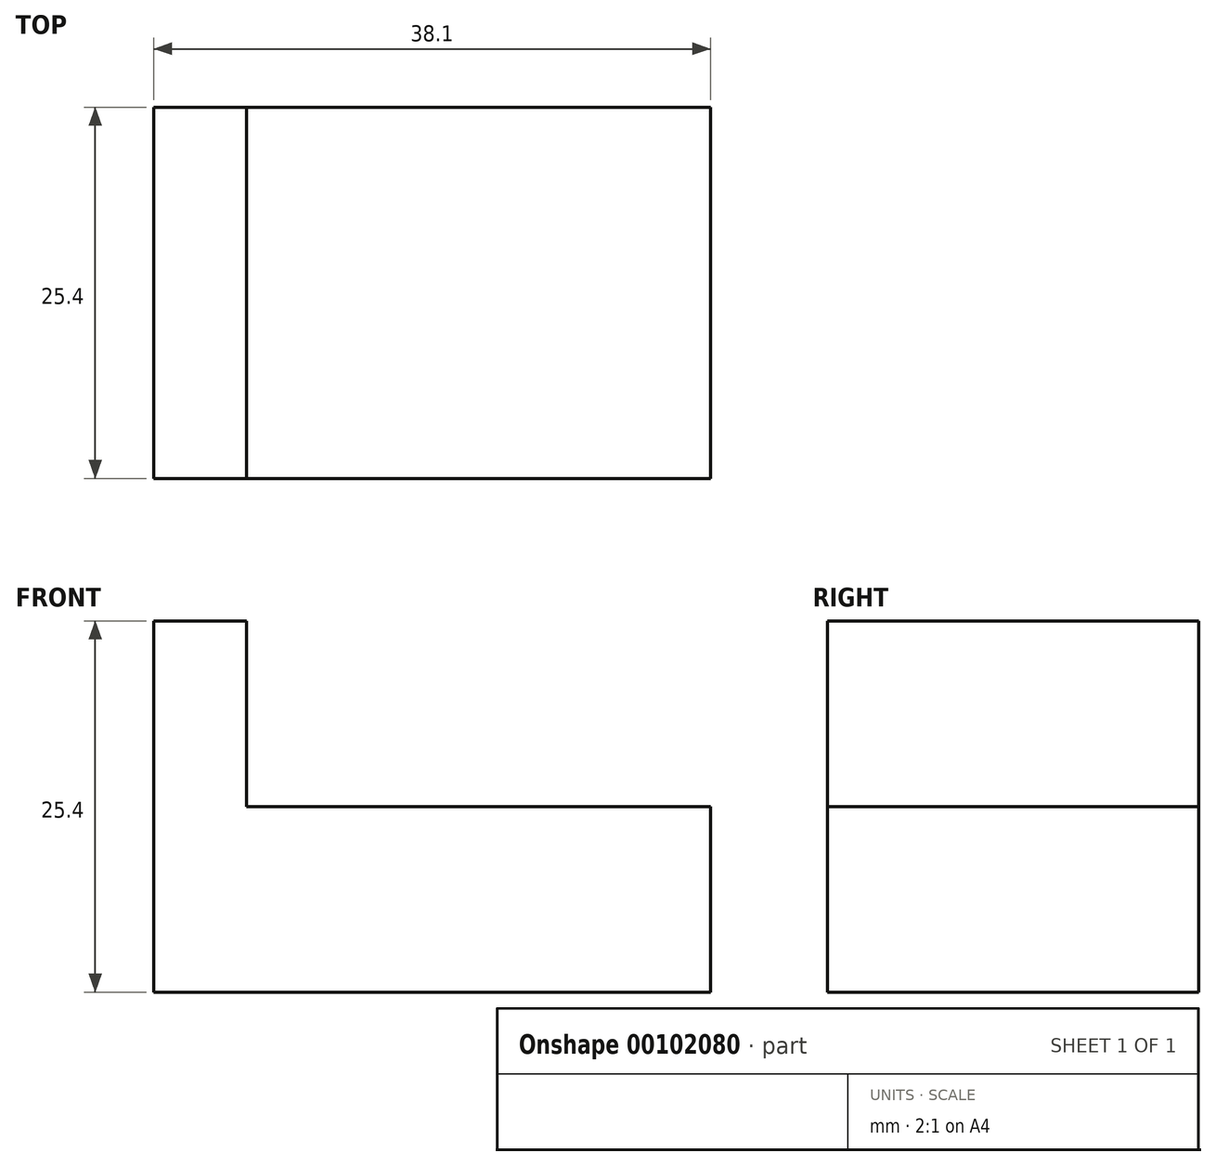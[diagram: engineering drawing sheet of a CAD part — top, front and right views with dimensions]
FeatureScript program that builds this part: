
annotation { "Feature Type Name" : "Feature", "Feature Type Description" : "" }
export const myFeature = defineFeature(function(context is Context, id is Id, definition is map)
    precondition{}
    {
        {
            var Q0;
            Q0=qCreatedBy(makeId("Front.planeOp"),FACE);
            var sketch = newSketch(context, id + "F0", { "sketchPlane" : qUnion([Q0])});
            skLineSegment(sketch, "E0", {"start": v(0, 25.4) * mm, "end": v(0, 0) * mm});
            skLineSegment(sketch, "E1", {"start": v(0, 0) * mm, "end": v(38.1, 0) * mm});
            skLineSegment(sketch, "E2", {"start": v(38.1, 0) * mm, "end": v(38.1, 12.7) * mm});
            skLineSegment(sketch, "E3", {"start": v(38.1, 12.7) * mm, "end": v(6.35, 12.7) * mm});
            skLineSegment(sketch, "E4", {"start": v(6.35, 12.7) * mm, "end": v(6.35, 25.4) * mm});
            skLineSegment(sketch, "E5", {"start": v(0, 25.4) * mm, "end": v(6.35, 25.4) * mm});
            skSolve(sketch);
        }
        {
            var Q0;
            Q0 = qSketchRegion(id + "F0", true);
            extrude(context, id + "F1", {"entities" : qUnion([Q0]), "depth" : 25.4 * mm});
        }
    });
